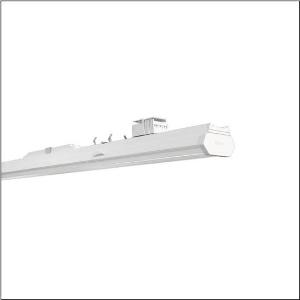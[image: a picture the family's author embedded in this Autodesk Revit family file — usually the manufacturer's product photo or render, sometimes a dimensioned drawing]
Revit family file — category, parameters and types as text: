
# Revit family: licross_r__21_protected_ho_52td11cn4c5s_1fd3
name_source: partatom
category: Lighting Fixtures
units: mm (PartAtom-declared; Revit-internal decimal feet)

## family parameters
Cut with Voids When Loaded = No
Host = Face
Light Source = No
Part Type = Normal
Room Calculation Point = No
Round Connector Dimension = Use Diameter
Shared = No

## types (1)
- --- (1 x LED, 12650 lm, 68.9 W, 4000K)
    Apparent Load = 69 VA
    CIE Flux Codes = 84 94 98 99 100
    Color Rendering = 80
    Color Temperature = 4000K
    Default Elevation = 1800 mm
    Description = Licross® 21 Protected HO, luminaire insert, of sheet steel, galvanised, coil coated, white, length: 1.500mm, width: 66mm, height: 67mm, LED rated luminous flux: 12.650lm, light colour: 840, control gear: ON/OFF Multilumen, CLOi, control gear: ECG Multilumen, with plug, 3-pole, with phase selection, mains connection: 220..240V, AC, 50/60Hz, start of lifetime: 69W, end of service life: 83W, halogen-free wiring, primary light control with lens, of plastic, primary optical cover: cover, of PMMA, light emission: direct distribution, primary light characteristic: symmetric, protection rating (complete): IP54, insulation class (complete): insulation class I (protective earthing), certification: CE, ENEC, VDE, UKCA, protection symbol: D if used in an environment with non-conductive dust loads with corresponding accessories, impact resistance: IK06, permissible ambient temperature for indoor applications: -35..+35°C, corresponds to IFS (International Featured Standards) requirements for safety and quality in the food industry, reducing of maximum allowable ambient temperature of 5°C with ceiling mounting, LABS conformity tested according to VDMA 24364:2018-05, packaging unit: 1 piece
    Height = 92 mm
    Lamp = 1 x LED
    Lamp Light Flux = 12650 lm
    Lamp Power = 68.9 W
    Lamp count = 1
    Length = 1500 mm
    Luminous efficacy = 184 lm/W
    Manufacturer = Siteco
    ModVariant = No
    Model = 52TD11CN4C5S
    Mounting Place = Ceiling
    Mounting Type = Pendant
    Number of Poles = 1
    OnlyDefault = Yes
    Power Factor = 1
    Product Name = Licross® 21 Protected HO
    Product group = luminaire insert
    ProductGroupID = 901
    Protection Class = Protection class I
    Protection Degree = IP 54
    RLX_Detail_Level = 1
    RLX_Emergency_Light_Flux = 0 lm
    RLX_Emergency_Type = 0
    RLX_Emergency_Type_DB = No
    RlxData = <blob elided: 22125 chars, md5=d7f6e929>
    Socket = socket
    Standby Power = 0 W
    System Light Flux = 12650 lm
    System Power = 69 W
    Type Comments = factory setting: luminous flux: 100 % | (A | C | E) | 162 mA
    Type Image = l_1256148.jpg
    URL = http://relux.com
    VarID = @adj_040993
    Voltage = 0 V
    Weight = 0.00 kg
    Width = 88 mm

## geometry (parser evidence)
native form markers: Blend x4, Sweep x12
no freeform markers — native parametric forms only
